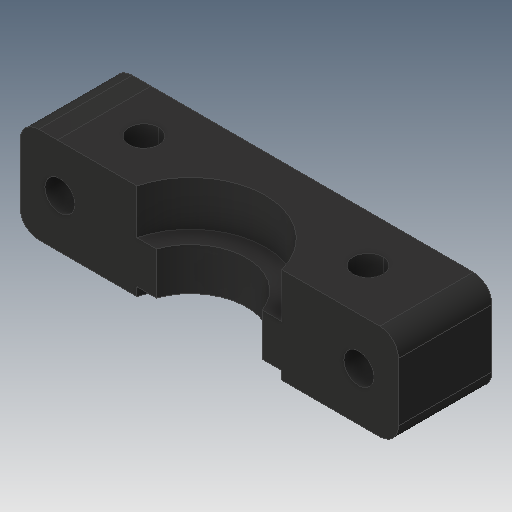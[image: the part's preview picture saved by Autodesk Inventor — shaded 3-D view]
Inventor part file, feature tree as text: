
AUTODESK INVENTOR PART (.ipt)
format: ipt  version: 2017 (Build 210142000, 142)  size: 248,320 bytes
history: native  units: in
note: dims shown in document units (in); Inventor stores cm internally (conversion verified against a paired STEP export)
features: sketch x9, extrude x7, projected_geometry x3, other x3, hole x1, reference x1
ambient origin geometry x8: Origin, YZ Plane, XZ Plane, XY Plane, X Axis, Y Axis, Z Axis, Center Point
bodies: Solid1 (feature_tree)
feature tree (24):
  extrude  "Extrusion1"  Depth=0.0787in
  extrude  "Extrusion2"  Depth=0.0787in
  extrude  "Extrusion3"  Depth=0.189in TaperAngle=0.0deg
  extrude  "Extrusion4"  Depth=0.189in TaperAngle=0.0deg
  hole  "Hole1"  [1 undecoded]
  extrude  "Extrusion5"  Depth=0.0394in
  sketch  "Sketch7"  dims[d17=0.0394in]
  sketch  "Sketch8"  dims[d18=0.126in d19=0.2362in d20=0.1575in d21=0.0787in d22=90.0deg d23=0.315in d24=0.8108in d25=0.1122in]
  extrude  "Extrusion6"  Depth=0.315in
  extrude  "Extrusion7"  Depth=0.1181in TaperAngle=0.0deg
  sketch  "Sketch1"  dims[d1=0.0787in d2=0.0787in]
  reference  "Reference1"
  sketch  "Sketch2"  dims[d3=0.3937in d4=0.0in d5=0.0787in]
  sketch  "Sketch3"  dims[d6=0.6299in d7=0.189in d8=0.0in]
  sketch  "Sketch4"  dims[d9=0.4724in d10=0.189in d11=0.0in]
  sketch  "Sketch5"  dims[d12=0.6299in d13=0.0354in d14=0.0in]
  sketch  "Sketch6"  dims[d15=0.1969in d16=0.0394in]
  projected_geometry  "Projected Loop1"
  projected_geometry  "Projected Loop2"
  sketch  "Sketch9"  dims[d26=0.1122in d27=0.1181in d28=0.0in d29=0.1181in d30=0.0in d31=0.1181in d32=0.0in]
  projected_geometry  "Projected Loop3"
  other  "<userpath>\OneDrive\Inventor\Beast 3D Printer\Hotend Mount Assembly.iam"
  other  "Hotend Mount Assembly.iam"
  other  "Hotend Slide Part 1:1"
note: 1 required parameter value undecoded (feature->parameter linkage not recoverable at this tier; creation-order binding heuristic only, values carry confidence <= 0.55)
